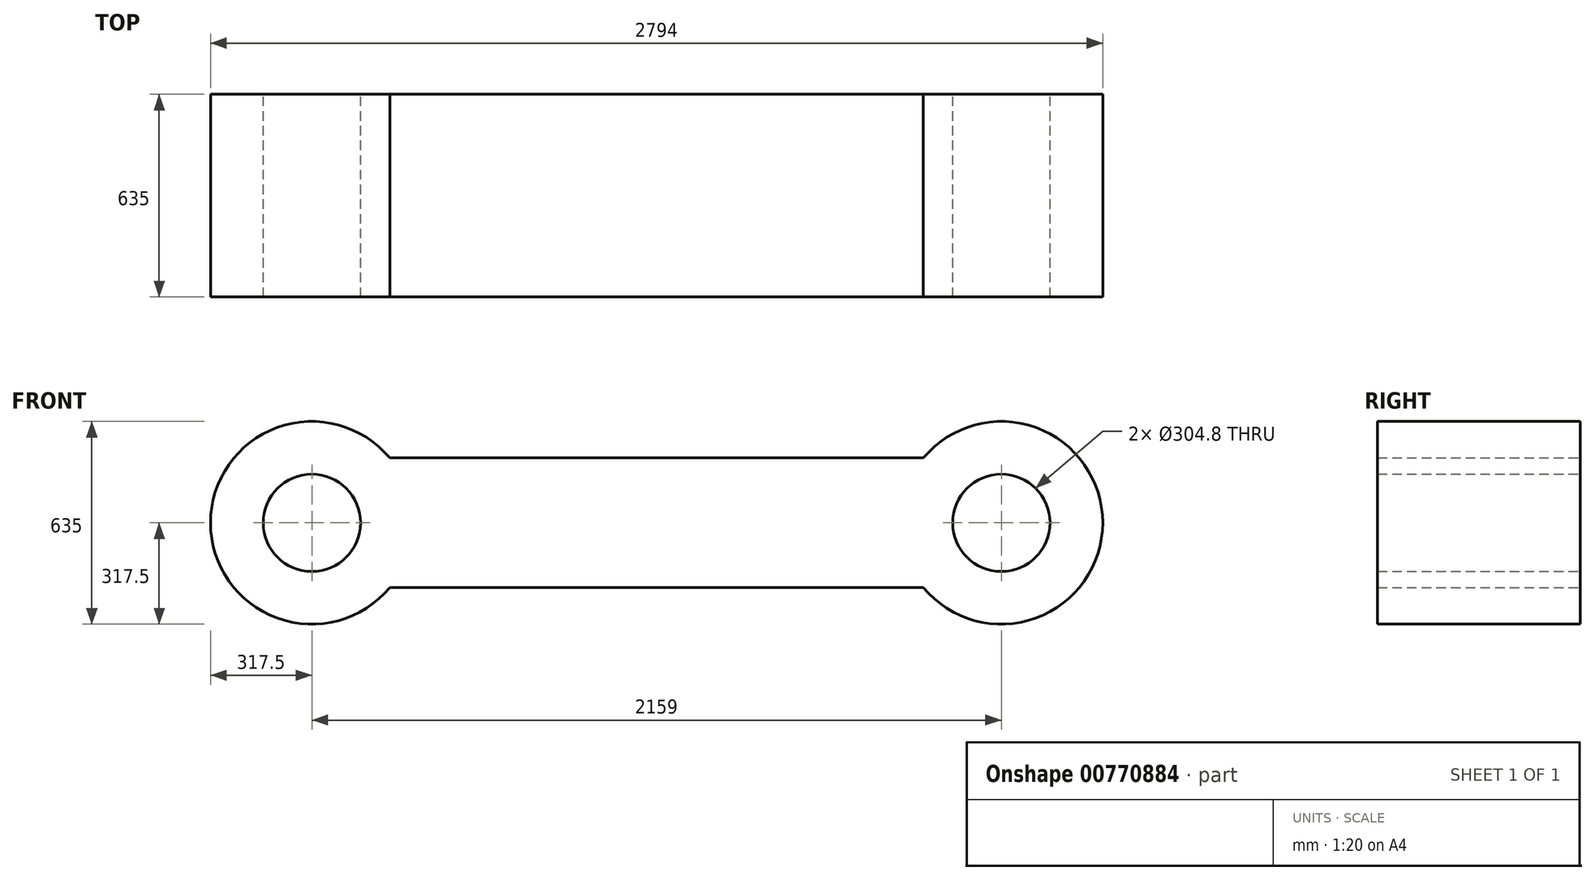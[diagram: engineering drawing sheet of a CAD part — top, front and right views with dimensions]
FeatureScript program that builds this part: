
annotation { "Feature Type Name" : "Feature", "Feature Type Description" : "" }
export const myFeature = defineFeature(function(context is Context, id is Id, definition is map)
    precondition{}
    {
        {
            var Q0;
            Q0=qCreatedBy(makeId("Front.planeOp"),FACE);
            var sketch = newSketch(context, id + "F0", { "sketchPlane" : qUnion([Q0])});
            skCircle(sketch, "E0", {"center": v(0, 0) * mm, "radius": 317.5 * mm});
            skCircle(sketch, "E1", {"center": v(2159, 0) * mm, "radius": 317.5 * mm});
            skLineSegment(sketch, "E2", {"start": v(0, 0) * mm, "end": v(2159, 0) * mm, "construction": true});
            skLineSegment(sketch, "E3", {"start": v(243.96, 203.2) * mm, "end": v(1915.04, 203.2) * mm});
            skLineSegment(sketch, "E4.MirrorCS", {"start": v(243.96, -203.2) * mm, "end": v(1915.04, -203.2) * mm});
            skCircle(sketch, "E5", {"center": v(0, 0) * mm, "radius": 152.4 * mm});
            skCircle(sketch, "E6", {"center": v(2159, 0) * mm, "radius": 152.4 * mm});
            skSolve(sketch);
        }
        {
            var Q0;
            Q0=qSketchRegion(id+"F0",true);
            extrude(context, id + "F1", {"entities" : qUnion([Q0]), "depth" : 635 * mm, "offsetDistance" : 25.4 * mm});
        }
    });
